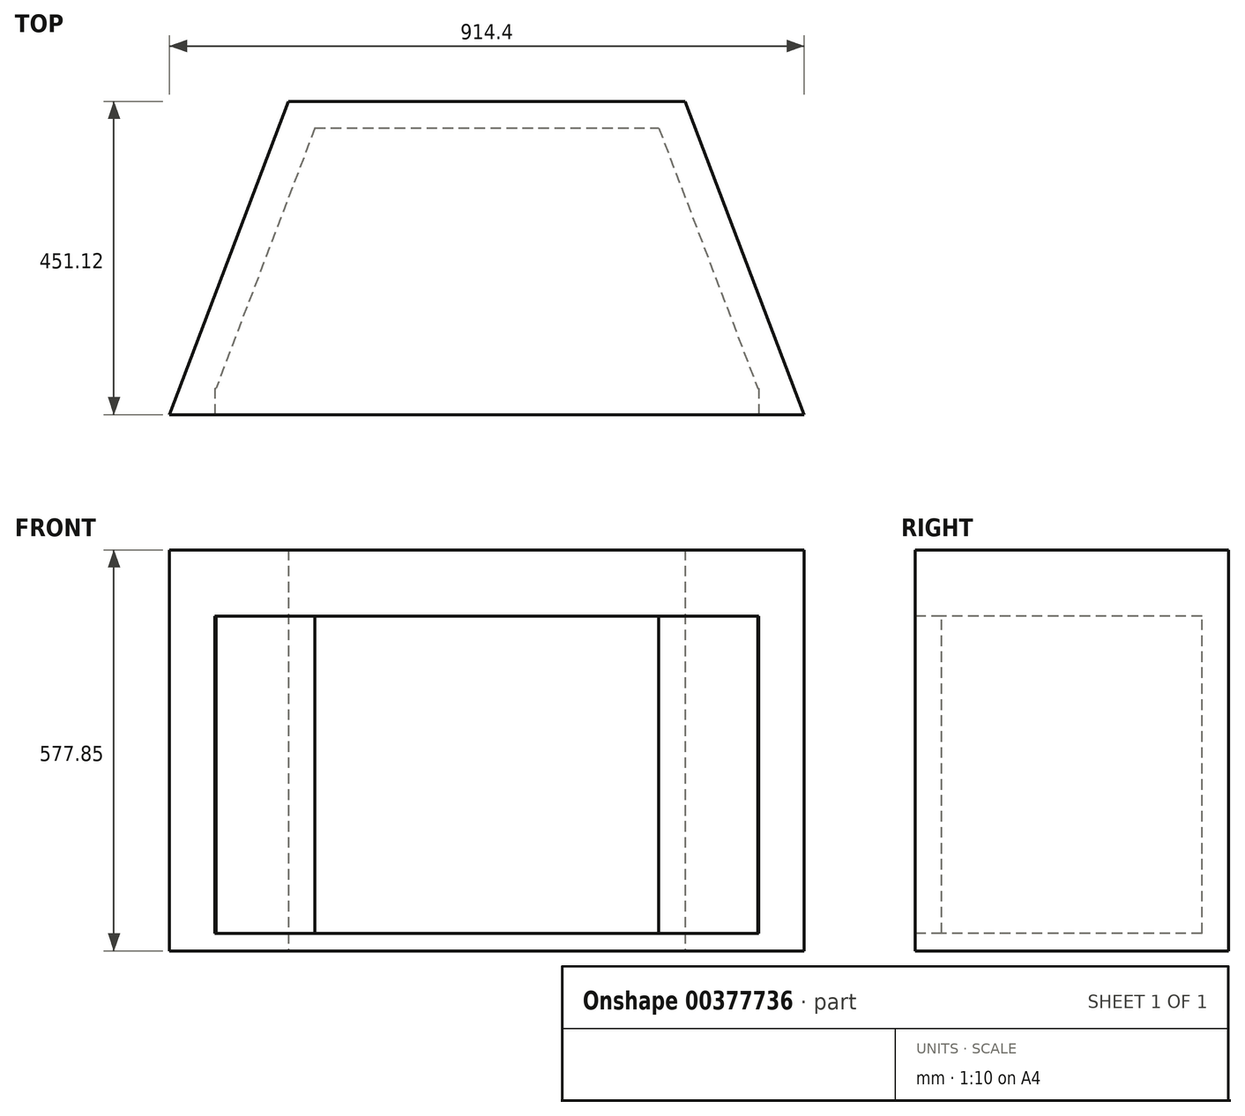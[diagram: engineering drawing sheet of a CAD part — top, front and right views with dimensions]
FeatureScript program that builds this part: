
annotation { "Feature Type Name" : "Feature", "Feature Type Description" : "" }
export const myFeature = defineFeature(function(context is Context, id is Id, definition is map)
    precondition{}
    {
        {
            var Q0;
            Q0=qCreatedBy(makeId("Top.planeOp"),FACE);
            var sketch = newSketch(context, id + "F0", { "sketchPlane" : qUnion([Q0])});
            skLineSegment(sketch, "E0", {"start": v(105.92, 263.8) * mm, "end": v(677.42, 263.8) * mm});
            skLineSegment(sketch, "E1", {"start": v(677.42, 263.8) * mm, "end": v(848.87, -187.32) * mm});
            skLineSegment(sketch, "E2", {"start": v(848.87, -187.32) * mm, "end": v(-65.53, -187.32) * mm});
            skLineSegment(sketch, "E3", {"start": v(-65.53, -187.32) * mm, "end": v(105.92, 263.8) * mm});
            skPoint(sketch, "E4.startSnap0", {"position": v(20.2, 38.24) * mm});
            skPoint(sketch, "E4.end.orphan", {"position": v(763.14, 38.24) * mm});
            skPoint(sketch, "E4.start.orphan", {"position": v(20.2, 0) * mm});
            skSolve(sketch);
        }
        {
            var Q0;
            Q0=makeQuery(id+"F0.imprint","IMPRINT",FACE,{"disambiguationData":[TD([[makeQuery(id+"F0.imprint","IMPRINT",EDGE,{"derivedFrom":sQuery(id+"F0.wireOp",EDGE,"E0")}),-1.0]])]});
            var sketch = newSketch(context, id + "F1", { "sketchPlane" : qUnion([Q0])});
            skSolve(sketch);
        }
        {
            var Q0;
            Q0 = qSketchRegion(id + "F1", true);
            var Q1;
            Q1=makeQuery(id+"F1.imprint","IMPRINT",FACE,{"disambiguationData":[TD([[makeQuery(id+"F1.imprint","IMPRINT",EDGE,{"derivedFrom":makeQuery(id+"F0.imprint","IMPRINT",EDGE,{"derivedFrom":sQuery(id+"F0.wireOp",EDGE,"E0")})}),-1.0]])]});
            extrude(context, id + "F2", {"entities" : qUnion([Q0, Q1]), "depth" : 482.6 * mm});
        }
        {
            var Q0;
            Q0=makeQuery(id+"F2.opExtrude","CAP_FACE",FACE,{"disambiguationData":[OSD([sQuery(id+"F0.wireOp",EDGE,"E0"),sQuery(id+"F0.wireOp",EDGE,"E1"),sQuery(id+"F0.wireOp",EDGE,"E2"),sQuery(id+"F0.wireOp",EDGE,"E3")])],"isStart":false});
            var sketch = newSketch(context, id + "F3", { "sketchPlane" : qUnion([Q0])});
            skLineSegment(sketch, "E5", {"start": v(144.02, 225.7) * mm, "end": v(639.32, 225.7) * mm});
            skLineSegment(sketch, "E6", {"start": v(639.32, 225.7) * mm, "end": v(781.8, -149.22) * mm});
            skLineSegment(sketch, "E7", {"start": v(1.53, -149.22) * mm, "end": v(781.8, -149.22) * mm});
            skLineSegment(sketch, "E8", {"start": v(144.02, 225.7) * mm, "end": v(1.53, -149.22) * mm});
            skPoint(sketch, "E9", {"position": v(391.67, 225.7) * mm});
            skPoint(sketch, "E10", {"position": v(391.67, -149.22) * mm});
            skPoint(sketch, "E11", {"position": v(391.67, 263.8) * mm});
            skPoint(sketch, "E12", {"position": v(391.67, -187.32) * mm});
            skPoint(sketch, "E13.orphan", {"position": v(91.44, 225.7) * mm});
            skPoint(sketch, "E14.orphan", {"position": v(-51.05, -149.22) * mm});
            skPoint(sketch, "E15.orphan", {"position": v(691.9, 225.7) * mm});
            skPoint(sketch, "E16.orphan", {"position": v(834.39, -149.22) * mm});
            skSolve(sketch);
        }
        {
            var Q0;
            Q0=makeQuery(id+"F3.imprint","IMPRINT",FACE,{"disambiguationData":[TD([[makeQuery(id+"F3.imprint","IMPRINT",EDGE,{"derivedFrom":sQuery(id+"F3.wireOp",EDGE,"E6")}),-1.0]])]});
            var sketch = newSketch(context, id + "F4", { "sketchPlane" : qUnion([Q0])});
            skSolve(sketch);
        }
        {
            var Q0;
            Q0 = qSketchRegion(id + "F4", true);
            var Q1;
            Q1=makeQuery(id+"F3.imprint","IMPRINT",FACE,{"disambiguationData":[TD([[makeQuery(id+"F3.imprint","IMPRINT",EDGE,{"derivedFrom":sQuery(id+"F3.wireOp",EDGE,"E6")}),1.0]])]});
            var Q2;
            Q2=makeQuery(id+"F3.imprint","IMPRINT",FACE,{"disambiguationData":[TD([[makeQuery(id+"F3.imprint","IMPRINT",EDGE,{"derivedFrom":sQuery(id+"F3.wireOp",EDGE,"E6")}),-1.0]])]});
            extrude(context, id + "F5", {"entities" : qUnion([Q0, Q1, Q2]), "operationType" : NewBodyOperationType.ADD, "depth" : 95.25 * mm});
        }
        {
            var Q0;
            Q0=makeQuery(id+"F4.imprint","IMPRINT",FACE,{"disambiguationData":[TD([[makeQuery(id+"F4.imprint","IMPRINT",EDGE,{"derivedFrom":makeQuery(id+"F3.imprint","IMPRINT",EDGE,{"derivedFrom":sQuery(id+"F3.wireOp",EDGE,"E6")})}),-1.0]])]});
            extrude(context, id + "F6", {"entities" : qUnion([Q0]), "operationType" : NewBodyOperationType.REMOVE, "oppositeDirection" : true, "depth" : 457.2 * mm});
        }
        {
            var Q0;
            {var subQ0=sQuery(id+"F0.wireOp",EDGE,"E2");Q0=makeQuery(id+"F5.boolean.opBoolean","MERGE",FACE,{"derivedFrom":[makeQuery(id+"F2.opExtrude","SWEPT_FACE",FACE,{"disambiguationData":[OSD([subQ0])]}),makeQuery(id+"F5.opExtrude","SWEPT_FACE",FACE,{"disambiguationData":[OSD([subQ0])]})]});}
            var sketch = newSketch(context, id + "F7", { "sketchPlane" : qUnion([Q0])});
            skPoint(sketch, "E17", {"position": v(391.67, 577.85) * mm});
            skPoint(sketch, "E18", {"position": v(1760.5, 813.4) * mm});
            skLineSegment(sketch, "E19", {"start": v(391.67, 577.85) * mm, "end": v(391.67, 0) * mm});
            skLineSegment(sketch, "E20.bottom", {"start": v(0, 482.6) * mm, "end": v(783.34, 482.6) * mm});
            skLineSegment(sketch, "E20.top", {"start": v(0, 25.4) * mm, "end": v(783.34, 25.4) * mm});
            skLineSegment(sketch, "E20.left", {"start": v(0, 482.6) * mm, "end": v(0, 25.4) * mm});
            skLineSegment(sketch, "E20.right", {"start": v(783.34, 482.6) * mm, "end": v(783.34, 25.4) * mm});
            skPoint(sketch, "E21", {"position": v(1729.36, 894.1) * mm});
            skPoint(sketch, "E21.positionSnap0", {"position": v(391.67, 25.4) * mm});
            skPoint(sketch, "E22", {"position": v(2185.55, 694.02) * mm});
            skLineSegment(sketch, "E23", {"start": v(-65.53, 25.4) * mm, "end": v(848.87, 25.4) * mm});
            skSolve(sketch);
        }
        {
            var Q0;
            Q0 = qSketchRegion(id + "F7", true);
            extrude(context, id + "F8", {"entities" : qUnion([Q0]), "operationType" : NewBodyOperationType.REMOVE, "oppositeDirection" : true, "depth" : 38.1 * mm});
        }
    });
